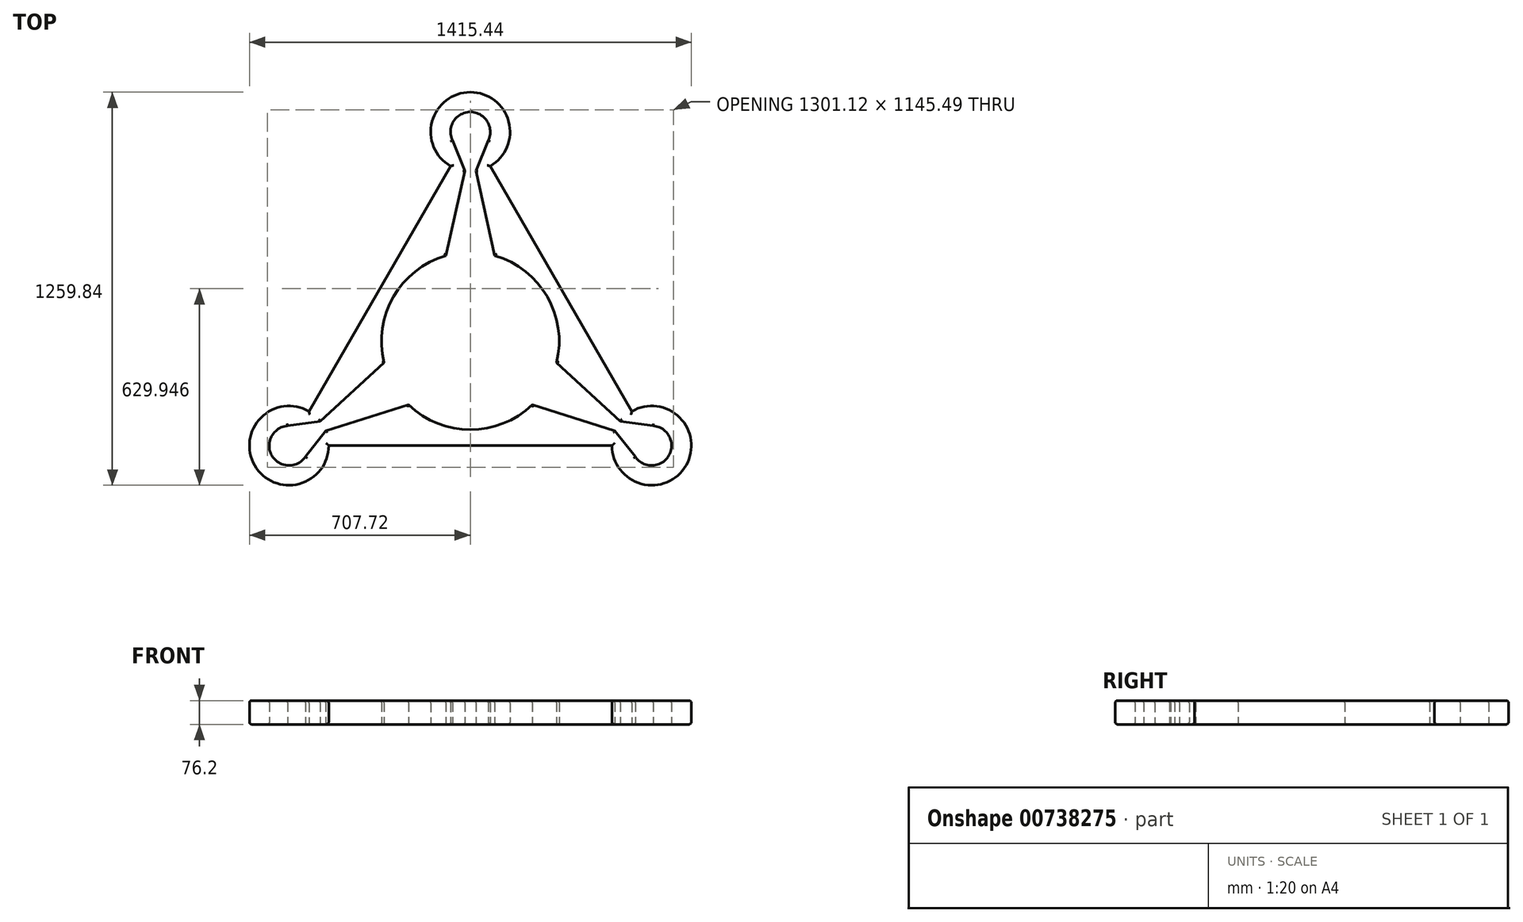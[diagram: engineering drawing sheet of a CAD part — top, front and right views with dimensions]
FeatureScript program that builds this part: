
annotation { "Feature Type Name" : "Feature", "Feature Type Description" : "" }
export const myFeature = defineFeature(function(context is Context, id is Id, definition is map)
    precondition{}
    {
        {
            var Q0;
            Q0=qCreatedBy(makeId("Top.planeOp"),FACE);
            var sketch = newSketch(context, id + "F0", { "sketchPlane" : qUnion([Q0])});
            skArc(sketch, "E0", {"start": v(-78.14, 273.54) * mm, "mid": v(-246.37, 142.24) * mm, "end": v(-275.96, -69.1) * mm});
            skPoint(sketch, "E1.0.midPoint", {"position": v(0, -335.28) * mm});
            skArc(sketch, "E2.cCircle", {"start": v(-78.14, 273.54) * mm, "mid": v(-246.37, 142.24) * mm, "end": v(-275.96, -69.1) * mm, "construction": true});
            skArc(sketch, "E3", {"start": v(-517.22, -225.3) * mm, "mid": v(-690.7, -398.78) * mm, "end": v(-453.72, -335.28) * mm});
            skArc(sketch, "E4", {"start": v(453.72, -335.28) * mm, "mid": v(690.7, -398.78) * mm, "end": v(517.22, -225.3) * mm});
            skLineSegment(sketch, "E5", {"start": v(-275.96, -69.1) * mm, "end": v(-480.7, -257) * mm});
            skLineSegment(sketch, "E6", {"start": v(-197.82, -204.44) * mm, "end": v(-462.93, -287.8) * mm});
            skLineSegment(sketch, "E7", {"start": v(197.82, -204.44) * mm, "end": v(462.93, -287.8) * mm});
            skLineSegment(sketch, "E8", {"start": v(275.96, -69.1) * mm, "end": v(480.7, -257) * mm});
            skArc(sketch, "E9", {"start": v(57.2, 642.97) * mm, "mid": v(0, 734.06) * mm, "end": v(-57.2, 642.97) * mm});
            skArc(sketch, "E10", {"start": v(528.23, -371.02) * mm, "mid": v(635.71, -367.03) * mm, "end": v(585.42, -271.95) * mm});
            skArc(sketch, "E11.cCircle", {"start": v(528.23, -371.02) * mm, "mid": v(563.35, -396.36) * mm, "end": v(606.55, -393.3) * mm, "construction": true});
            skLineSegment(sketch, "E12", {"start": v(462.93, -287.8) * mm, "end": v(533.53, -377.77) * mm});
            skLineSegment(sketch, "E13", {"start": v(480.7, -257) * mm, "end": v(593.92, -273.17) * mm});
            skArc(sketch, "E14.cCircle", {"start": v(-585.42, -271.95) * mm, "mid": v(-635.71, -367.03) * mm, "end": v(-528.23, -371.02) * mm, "construction": true});
            skLineSegment(sketch, "E15", {"start": v(-593.92, -273.17) * mm, "end": v(-480.7, -257) * mm});
            skLineSegment(sketch, "E16", {"start": v(-533.53, -377.77) * mm, "end": v(-462.93, -287.8) * mm});
            skArc(sketch, "E17.cCircle", {"start": v(57.2, 642.97) * mm, "mid": v(0, 734.06) * mm, "end": v(-57.2, 642.97) * mm, "construction": true});
            skLineSegment(sketch, "E18", {"start": v(-60.4, 650.94) * mm, "end": v(-17.78, 544.81) * mm});
            skLineSegment(sketch, "E19", {"start": v(60.4, 650.94) * mm, "end": v(17.78, 544.81) * mm});
            skPoint(sketch, "E20.0.start.orphan", {"position": v(0, 142.24) * mm});
            skLineSegment(sketch, "E21.trimOffspring", {"start": v(78.14, 273.54) * mm, "end": v(17.78, 544.81) * mm});
            skLineSegment(sketch, "E22.trimOffspring", {"start": v(-78.14, 273.54) * mm, "end": v(-17.78, 544.81) * mm});
            skPoint(sketch, "E23.orphan", {"position": v(-246.37, 142.24) * mm});
            skPoint(sketch, "E24.orphan", {"position": v(246.37, 142.24) * mm});
            skPoint(sketch, "E25.orphan", {"position": v(0, -284.48) * mm});
            skArc(sketch, "E26.trimOffspring", {"start": v(-197.82, -204.44) * mm, "mid": v(0, -284.48) * mm, "end": v(197.82, -204.44) * mm, "construction": true});
            skArc(sketch, "E27.trimOffspring", {"start": v(-197.82, -204.44) * mm, "mid": v(0, -284.48) * mm, "end": v(197.82, -204.44) * mm});
            skArc(sketch, "E28.trimOffspring", {"start": v(275.96, -69.1) * mm, "mid": v(246.37, 142.24) * mm, "end": v(78.14, 273.54) * mm, "construction": true});
            skArc(sketch, "E29.trimOffspring", {"start": v(275.96, -69.1) * mm, "mid": v(246.37, 142.24) * mm, "end": v(78.14, 273.54) * mm});
            skLineSegment(sketch, "E30.trimOffspring", {"start": v(453.72, -335.28) * mm, "end": v(-453.72, -335.28) * mm});
            skArc(sketch, "E31.trimOffspring", {"start": v(643.87, -328.64) * mm, "mid": v(624.93, -289.7) * mm, "end": v(585.42, -271.95) * mm, "construction": true});
            skLineSegment(sketch, "E32.trimOffspring", {"start": v(-517.22, -225.3) * mm, "end": v(-63.5, 560.57) * mm});
            skArc(sketch, "E33.trimOffspring", {"start": v(-585.42, -271.95) * mm, "mid": v(-635.71, -367.03) * mm, "end": v(-528.23, -371.02) * mm});
            skLineSegment(sketch, "E34.trimOffspring", {"start": v(63.5, 560.57) * mm, "end": v(517.22, -225.3) * mm});
            skArc(sketch, "E35.trimOffspring", {"start": v(63.5, 560.57) * mm, "mid": v(0, 797.56) * mm, "end": v(-63.5, 560.57) * mm});
            skSolve(sketch);
        }
        {
            var Q0;
            Q0=makeQuery(id+"F0.imprint","IMPRINT",FACE,{"disambiguationData":[TD([[makeQuery(id+"F0.imprint","IMPRINT",EDGE,{"derivedFrom":sQuery(id+"F0.wireOp",EDGE,"E0")}),-1.0]])]});
            extrude(context, id + "F1", {"entities" : qUnion([Q0]), "depth" : 76.2 * mm, "offsetDistance" : 25.4 * mm});
        }
        {
            var Q0;
            Q0=makeQuery(id+"F1.opExtrude","CAP_EDGE",EDGE,{"disambiguationData":[OSD([sQuery(id+"F0.wireOp",EDGE,"E9")])],"isStart":false});
            var Q1;
            Q1=makeQuery(id+"F1.opExtrude","CAP_EDGE",EDGE,{"disambiguationData":[OSD([sQuery(id+"F0.wireOp",EDGE,"E18")])],"isStart":false});
            var Q2;
            Q2=makeQuery(id+"F1.opExtrude","CAP_EDGE",EDGE,{"disambiguationData":[OSD([sQuery(id+"F0.wireOp",EDGE,"E19")])],"isStart":false});
            var Q3;
            Q3=makeQuery(id+"F1.opExtrude","CAP_EDGE",EDGE,{"disambiguationData":[OSD([sQuery(id+"F0.wireOp",EDGE,"E22.trimOffspring")])],"isStart":false});
            var Q4;
            Q4=makeQuery(id+"F1.opExtrude","CAP_EDGE",EDGE,{"disambiguationData":[OSD([sQuery(id+"F0.wireOp",EDGE,"E21.trimOffspring")])],"isStart":false});
            var Q5;
            Q5=makeQuery(id+"F1.opExtrude","CAP_EDGE",EDGE,{"disambiguationData":[OSD([sQuery(id+"F0.wireOp",EDGE,"E0")])],"isStart":false});
            var Q6;
            Q6=makeQuery(id+"F1.opExtrude","CAP_EDGE",EDGE,{"disambiguationData":[OSD([sQuery(id+"F0.wireOp",EDGE,"E29.trimOffspring")])],"isStart":false});
            var Q7;
            Q7=makeQuery(id+"F1.opExtrude","CAP_EDGE",EDGE,{"disambiguationData":[OSD([sQuery(id+"F0.wireOp",EDGE,"E8")])],"isStart":false});
            var Q8;
            Q8=makeQuery(id+"F1.opExtrude","CAP_EDGE",EDGE,{"disambiguationData":[OSD([sQuery(id+"F0.wireOp",EDGE,"E13")])],"isStart":false});
            var Q9;
            Q9=makeQuery(id+"F1.opExtrude","CAP_EDGE",EDGE,{"disambiguationData":[OSD([sQuery(id+"F0.wireOp",EDGE,"E10")])],"isStart":false});
            var Q10;
            Q10=makeQuery(id+"F1.opExtrude","CAP_EDGE",EDGE,{"disambiguationData":[OSD([sQuery(id+"F0.wireOp",EDGE,"E12")])],"isStart":false});
            var Q11;
            Q11=makeQuery(id+"F1.opExtrude","CAP_EDGE",EDGE,{"disambiguationData":[OSD([sQuery(id+"F0.wireOp",EDGE,"E7")])],"isStart":false});
            var Q12;
            Q12=makeQuery(id+"F1.opExtrude","CAP_EDGE",EDGE,{"disambiguationData":[OSD([sQuery(id+"F0.wireOp",EDGE,"E27.trimOffspring")])],"isStart":false});
            var Q13;
            Q13=makeQuery(id+"F1.opExtrude","CAP_EDGE",EDGE,{"disambiguationData":[OSD([sQuery(id+"F0.wireOp",EDGE,"E5")])],"isStart":false});
            var Q14;
            Q14=makeQuery(id+"F1.opExtrude","CAP_EDGE",EDGE,{"disambiguationData":[OSD([sQuery(id+"F0.wireOp",EDGE,"E6")])],"isStart":false});
            var Q15;
            Q15=makeQuery(id+"F1.opExtrude","CAP_EDGE",EDGE,{"disambiguationData":[OSD([sQuery(id+"F0.wireOp",EDGE,"E15")])],"isStart":false});
            var Q16;
            Q16=makeQuery(id+"F1.opExtrude","CAP_EDGE",EDGE,{"disambiguationData":[OSD([sQuery(id+"F0.wireOp",EDGE,"E33.trimOffspring")])],"isStart":false});
            var Q17;
            Q17=makeQuery(id+"F1.opExtrude","CAP_EDGE",EDGE,{"disambiguationData":[OSD([sQuery(id+"F0.wireOp",EDGE,"E16")])],"isStart":false});
            fillet(context, id + "F2", {"entities" : qUnion([Q0, Q1, Q2, Q3, Q4, Q5, Q6, Q7, Q8, Q9, Q10, Q11, Q12, Q13, Q14, Q15, Q16, Q17]), "radius" : 6.35 * mm, "tangentPropagation" : true, "allowEdgeOverflow" : false});
        }
        {
            var Q0;
            Q0=makeQuery(id+"F1.opExtrude","CAP_EDGE",EDGE,{"disambiguationData":[OSD([sQuery(id+"F0.wireOp",EDGE,"E10")])],"isStart":true});
            var Q1;
            Q1=makeQuery(id+"F1.opExtrude","CAP_EDGE",EDGE,{"disambiguationData":[OSD([sQuery(id+"F0.wireOp",EDGE,"E13")])],"isStart":true});
            var Q2;
            Q2=makeQuery(id+"F1.opExtrude","CAP_EDGE",EDGE,{"disambiguationData":[OSD([sQuery(id+"F0.wireOp",EDGE,"E8")])],"isStart":true});
            var Q3;
            Q3=makeQuery(id+"F1.opExtrude","CAP_EDGE",EDGE,{"disambiguationData":[OSD([sQuery(id+"F0.wireOp",EDGE,"E12")])],"isStart":true});
            var Q4;
            Q4=makeQuery(id+"F1.opExtrude","CAP_EDGE",EDGE,{"disambiguationData":[OSD([sQuery(id+"F0.wireOp",EDGE,"E7")])],"isStart":true});
            var Q5;
            Q5=makeQuery(id+"F1.opExtrude","CAP_EDGE",EDGE,{"disambiguationData":[OSD([sQuery(id+"F0.wireOp",EDGE,"E21.trimOffspring")])],"isStart":true});
            var Q6;
            Q6=makeQuery(id+"F1.opExtrude","CAP_EDGE",EDGE,{"disambiguationData":[OSD([sQuery(id+"F0.wireOp",EDGE,"E18")])],"isStart":true});
            var Q7;
            Q7=makeQuery(id+"F1.opExtrude","CAP_EDGE",EDGE,{"disambiguationData":[OSD([sQuery(id+"F0.wireOp",EDGE,"E22.trimOffspring")])],"isStart":true});
            var Q8;
            Q8=makeQuery(id+"F1.opExtrude","CAP_EDGE",EDGE,{"disambiguationData":[OSD([sQuery(id+"F0.wireOp",EDGE,"E0")])],"isStart":true});
            var Q9;
            Q9=makeQuery(id+"F1.opExtrude","CAP_EDGE",EDGE,{"disambiguationData":[OSD([sQuery(id+"F0.wireOp",EDGE,"E5")])],"isStart":true});
            var Q10;
            Q10=makeQuery(id+"F1.opExtrude","CAP_EDGE",EDGE,{"disambiguationData":[OSD([sQuery(id+"F0.wireOp",EDGE,"E6")])],"isStart":true});
            var Q11;
            Q11=makeQuery(id+"F1.opExtrude","CAP_EDGE",EDGE,{"disambiguationData":[OSD([sQuery(id+"F0.wireOp",EDGE,"E15")])],"isStart":true});
            var Q12;
            Q12=makeQuery(id+"F1.opExtrude","CAP_EDGE",EDGE,{"disambiguationData":[OSD([sQuery(id+"F0.wireOp",EDGE,"E19")])],"isStart":true});
            var Q13;
            Q13=makeQuery(id+"F1.opExtrude","CAP_EDGE",EDGE,{"disambiguationData":[OSD([sQuery(id+"F0.wireOp",EDGE,"E9")])],"isStart":true});
            var Q14;
            Q14=makeQuery(id+"F1.opExtrude","CAP_EDGE",EDGE,{"disambiguationData":[OSD([sQuery(id+"F0.wireOp",EDGE,"E33.trimOffspring")])],"isStart":true});
            var Q15;
            Q15=makeQuery(id+"F1.opExtrude","CAP_EDGE",EDGE,{"disambiguationData":[OSD([sQuery(id+"F0.wireOp",EDGE,"E16")])],"isStart":true});
            var Q16;
            Q16=makeQuery(id+"F1.opExtrude","CAP_EDGE",EDGE,{"disambiguationData":[OSD([sQuery(id+"F0.wireOp",EDGE,"E27.trimOffspring")])],"isStart":true});
            var Q17;
            Q17=makeQuery(id+"F1.opExtrude","CAP_EDGE",EDGE,{"disambiguationData":[OSD([sQuery(id+"F0.wireOp",EDGE,"E29.trimOffspring")])],"isStart":true});
            fillet(context, id + "F3", {"entities" : qUnion([Q0, Q1, Q2, Q3, Q4, Q5, Q6, Q7, Q8, Q9, Q10, Q11, Q12, Q13, Q14, Q15, Q16, Q17]), "radius" : 6.35 * mm, "tangentPropagation" : true, "allowEdgeOverflow" : false});
        }
        {
            var Q0;
            Q0=makeQuery(id+"F1.opExtrude","CAP_EDGE",EDGE,{"disambiguationData":[OSD([sQuery(id+"F0.wireOp",EDGE,"E34.trimOffspring")])],"isStart":true});
            var Q1;
            Q1=makeQuery(id+"F1.opExtrude","CAP_EDGE",EDGE,{"disambiguationData":[OSD([sQuery(id+"F0.wireOp",EDGE,"E34.trimOffspring")])],"isStart":false});
            var Q2;
            Q2=makeQuery(id+"F1.opExtrude","CAP_EDGE",EDGE,{"disambiguationData":[OSD([sQuery(id+"F0.wireOp",EDGE,"E30.trimOffspring")])],"isStart":true});
            var Q3;
            Q3=makeQuery(id+"F1.opExtrude","CAP_EDGE",EDGE,{"disambiguationData":[OSD([sQuery(id+"F0.wireOp",EDGE,"E30.trimOffspring")])],"isStart":false});
            var Q4;
            Q4=makeQuery(id+"F1.opExtrude","CAP_EDGE",EDGE,{"disambiguationData":[OSD([sQuery(id+"F0.wireOp",EDGE,"E32.trimOffspring")])],"isStart":true});
            var Q5;
            Q5=makeQuery(id+"F1.opExtrude","CAP_EDGE",EDGE,{"disambiguationData":[OSD([sQuery(id+"F0.wireOp",EDGE,"E32.trimOffspring")])],"isStart":false});
            var Q6;
            Q6=makeQuery(id+"F1.opExtrude","CAP_EDGE",EDGE,{"disambiguationData":[OSD([sQuery(id+"F0.wireOp",EDGE,"E3")])],"isStart":false});
            var Q7;
            Q7=makeQuery(id+"F1.opExtrude","CAP_EDGE",EDGE,{"disambiguationData":[OSD([sQuery(id+"F0.wireOp",EDGE,"E3")])],"isStart":true});
            var Q8;
            Q8=makeQuery(id+"F1.opExtrude","CAP_EDGE",EDGE,{"disambiguationData":[OSD([sQuery(id+"F0.wireOp",EDGE,"E35.trimOffspring")])],"isStart":true});
            var Q9;
            Q9=makeQuery(id+"F1.opExtrude","CAP_EDGE",EDGE,{"disambiguationData":[OSD([sQuery(id+"F0.wireOp",EDGE,"E35.trimOffspring")])],"isStart":false});
            var Q10;
            Q10=makeQuery(id+"F1.opExtrude","CAP_EDGE",EDGE,{"disambiguationData":[OSD([sQuery(id+"F0.wireOp",EDGE,"E4")])],"isStart":true});
            var Q11;
            Q11=makeQuery(id+"F1.opExtrude","CAP_EDGE",EDGE,{"disambiguationData":[OSD([sQuery(id+"F0.wireOp",EDGE,"E4")])],"isStart":false});
            fillet(context, id + "F4", {"entities" : qUnion([Q0, Q1, Q2, Q3, Q4, Q5, Q6, Q7, Q8, Q9, Q10, Q11]), "radius" : 7.62 * mm, "tangentPropagation" : true, "allowEdgeOverflow" : false});
        }
    });
